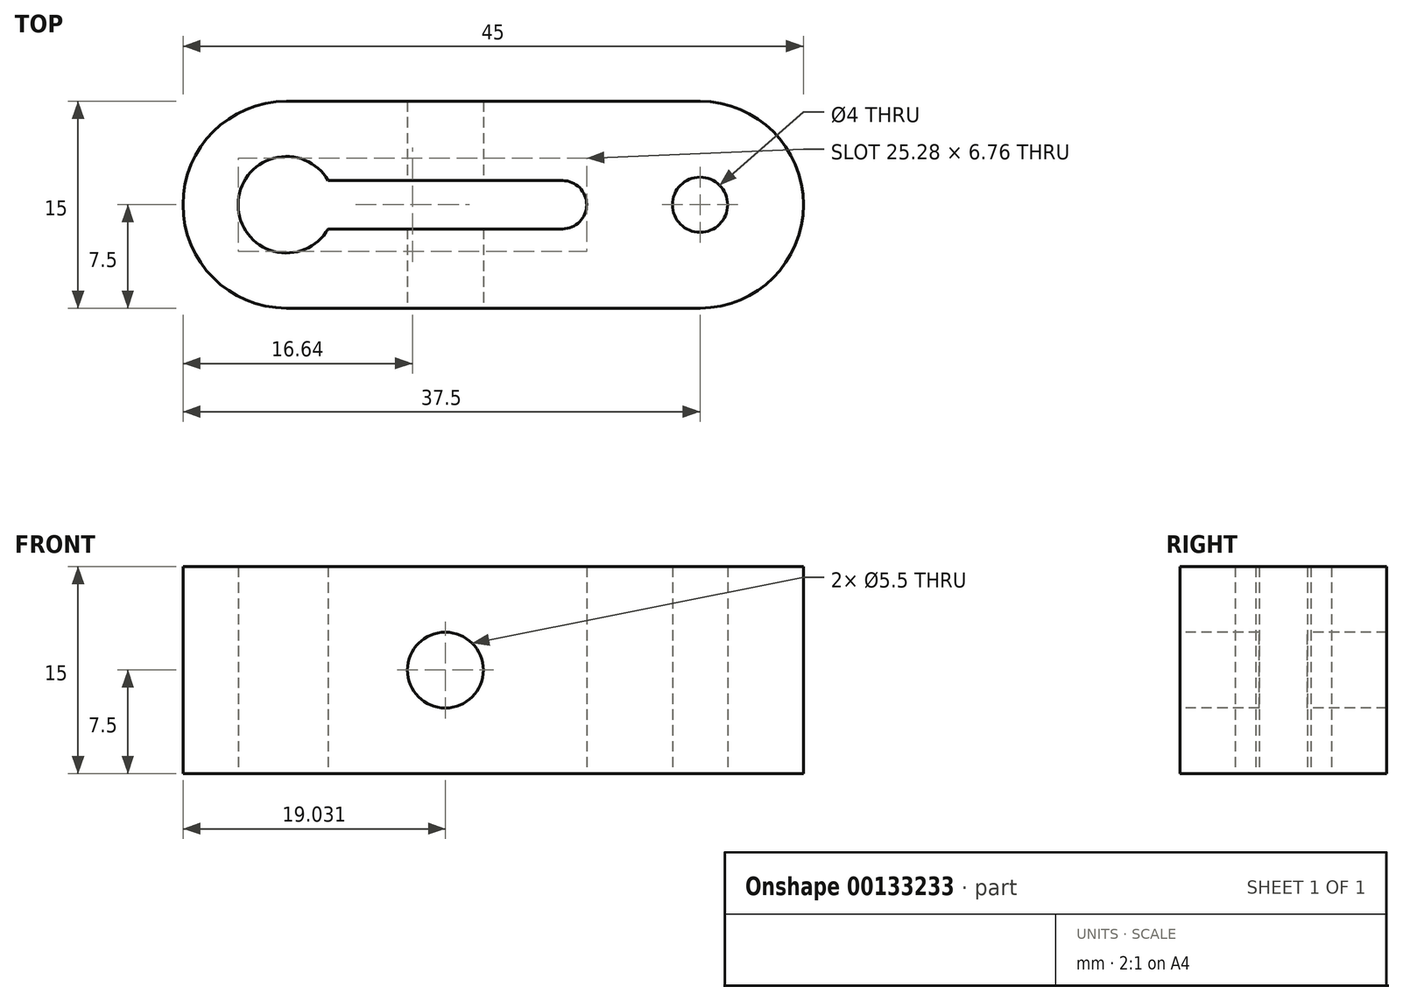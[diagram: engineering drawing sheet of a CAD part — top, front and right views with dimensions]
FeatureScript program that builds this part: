
annotation { "Feature Type Name" : "Feature", "Feature Type Description" : "" }
export const myFeature = defineFeature(function(context is Context, id is Id, definition is map)
    precondition{}
    {
        {
            var Q0;
            Q0=qCreatedBy(makeId("Top.planeOp"),FACE);
            var sketch = newSketch(context, id + "F0", { "sketchPlane" : qUnion([Q0])});
            skCircle(sketch, "E0", {"center": v(30, 0) * mm, "radius": 7.5 * mm});
            skCircle(sketch, "E1", {"center": v(0, 0) * mm, "radius": 7.5 * mm});
            skLineSegment(sketch, "E2", {"start": v(0, 7.5) * mm, "end": v(30, 7.5) * mm});
            skLineSegment(sketch, "E3", {"start": v(30, -7.5) * mm, "end": v(0, -7.5) * mm});
            skCircle(sketch, "E4", {"center": v(0, 0) * mm, "radius": 3.5 * mm});
            skCircle(sketch, "E5", {"center": v(30, 0) * mm, "radius": 2 * mm});
            skArc(sketch, "E6", {"start": v(20.03, 1.75) * mm, "mid": v(21.78, 0) * mm, "end": v(20.03, -1.75) * mm});
            skLineSegment(sketch, "E7", {"start": v(20.03, -1.75) * mm, "end": v(3.03, -1.75) * mm});
            skLineSegment(sketch, "E8.MirrorCS", {"start": v(20.03, 1.75) * mm, "end": v(3.03, 1.75) * mm});
            skSolve(sketch);
        }
        {
            var Q0;
            {var subQ5=sQuery(id+"F0.wireOp",EDGE,"E1");var subQ8=makeQuery(id+"F0.imprint","INTERSECT",VERTEX,{"derivedFrom":[subQ5,sQuery(id+"F0.wireOp",EDGE,"E2")]});Q0=makeQuery(id+"F0.imprint","IMPRINT",FACE,{"disambiguationData":[TD([[makeQuery(id+"F0.imprint","IMPRINT",EDGE,{"disambiguationData":[TD([[subQ8,1.0]])],"derivedFrom":subQ5}),1.0]])]});}
            var Q1;
            {var subQ0=sQuery(id+"F0.wireOp",EDGE,"E2");Q1=makeQuery(id+"F0.imprint","IMPRINT",FACE,{"disambiguationData":[TD([[makeQuery(id+"F0.imprint","IMPRINT",EDGE,{"derivedFrom":subQ0}),-1.0]])]});}
            var Q2;
            Q2=makeQuery(id+"F0.imprint","IMPRINT",FACE,{"disambiguationData":[TD([[makeQuery(id+"F0.imprint","IMPRINT",EDGE,{"derivedFrom":sQuery(id+"F0.wireOp",EDGE,"E5")}),-1.0]])]});
            extrude(context, id + "F1", {"entities" : qUnion([Q0, Q1, Q2]), "depth" : 15 * mm});
        }
        {
            var Q0;
            Q0=makeQuery(id+"F1.opExtrude","SWEPT_FACE",FACE,{"disambiguationData":[OSD([sQuery(id+"F0.wireOp",EDGE,"E3")])]});
            var sketch = newSketch(context, id + "F2", { "sketchPlane" : qUnion([Q0])});
            skLineSegment(sketch, "E9", {"start": v(3.03, 15) * mm, "end": v(20.03, 0) * mm, "construction": true});
            skCircle(sketch, "E10", {"center": v(11.53, 7.5) * mm, "radius": 2.75 * mm});
            skSolve(sketch);
        }
        {
            var Q0;
            Q0=makeQuery(id+"F2.imprint","IMPRINT",FACE,{"disambiguationData":[TD([[makeQuery(id+"F2.imprint","IMPRINT",EDGE,{"derivedFrom":sQuery(id+"F2.wireOp",EDGE,"E10")}),1.0]])]});
            extrude(context, id + "F3", {"entities" : qUnion([Q0]), "operationType" : NewBodyOperationType.REMOVE, "endBound" : BoundingType.THROUGH_ALL, "oppositeDirection" : true, "depth" : 25 * mm});
        }
    });
